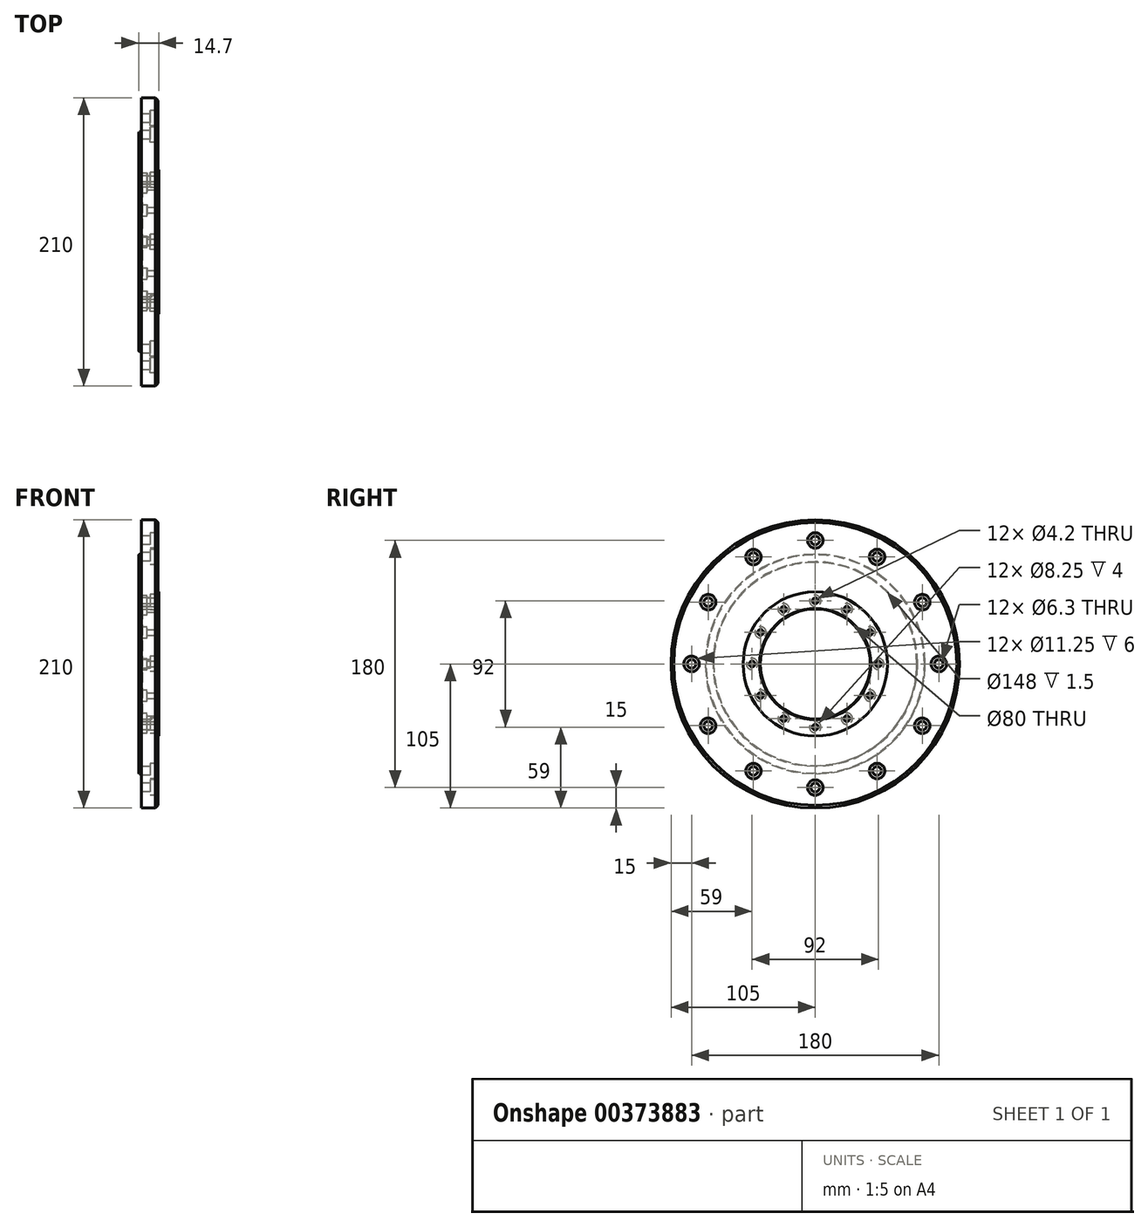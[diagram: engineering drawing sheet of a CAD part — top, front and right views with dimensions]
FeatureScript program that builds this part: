
annotation { "Feature Type Name" : "Feature", "Feature Type Description" : "" }
export const myFeature = defineFeature(function(context is Context, id is Id, definition is map)
    precondition{}
    {
        {
            var Q0;
            Q0=qCreatedBy(makeId("Front.planeOp"),FACE);
            var sketch = newSketch(context, id + "F0", { "sketchPlane" : qUnion([Q0])});
            skLineSegment(sketch, "E0", {"start": v(91.08, 0) * mm, "end": v(-135.26, 0) * mm, "construction": true});
            skLineSegment(sketch, "E1", {"start": v(-4.62, 80) * mm, "end": v(-4.62, 105) * mm});
            skLineSegment(sketch, "E2", {"start": v(-4.62, 105) * mm, "end": v(7.58, 105) * mm});
            skLineSegment(sketch, "E3", {"start": v(7.58, 105) * mm, "end": v(7.58, 52.5) * mm});
            skLineSegment(sketch, "E4", {"start": v(7.58, 52.5) * mm, "end": v(8.08, 52.5) * mm});
            skLineSegment(sketch, "E5", {"start": v(8.08, 52.5) * mm, "end": v(8.08, 40) * mm});
            skLineSegment(sketch, "E6", {"start": v(-4.62, 80) * mm, "end": v(-6.62, 80) * mm});
            skLineSegment(sketch, "E7", {"start": v(8.08, 40) * mm, "end": v(-4.62, 40) * mm});
            skLineSegment(sketch, "E8", {"start": v(-6.62, 80) * mm, "end": v(-6.62, 74) * mm});
            skLineSegment(sketch, "E9", {"start": v(-6.62, 74) * mm, "end": v(-4.62, 74) * mm});
            skLineSegment(sketch, "E10", {"start": v(-4.62, 74) * mm, "end": v(-4.62, 40) * mm});
            skPoint(sketch, "E11.orphan", {"position": v(-6.62, 40) * mm});
            skSolve(sketch);
        }
        {
            var Q0;
            Q0 = qSketchRegion(id + "F0", true);
            var Q1;
            Q1=sQuery(id+"F0.wireOp",EDGE,"E0");
            revolve(context, id + "F1", {"entities" : qUnion([Q0]), "axis" : qUnion([Q1]), "revolveType" : RevolveType.FULL});
        }
        {
            var Q0;
            Q0=makeQuery(id+"F1.opRevolve","SWEPT_FACE",FACE,{"disambiguationData":[OSD([sQuery(id+"F0.wireOp",EDGE,"E1")])]});
            var sketch = newSketch(context, id + "F2", { "sketchPlane" : qUnion([Q0])});
            skPoint(sketch, "E12", {"position": v(0, 0) * mm});
            skPoint(sketch, "E13", {"position": v(0, 46) * mm});
            skPoint(sketch, "E14", {"position": v(23, 39.84) * mm});
            skPoint(sketch, "E15", {"position": v(39.84, 23) * mm});
            skPoint(sketch, "E16", {"position": v(46, 0) * mm});
            skPoint(sketch, "E17", {"position": v(39.84, -23) * mm});
            skPoint(sketch, "E18", {"position": v(23, -39.84) * mm});
            skPoint(sketch, "E19", {"position": v(0, -46) * mm});
            skPoint(sketch, "E20", {"position": v(-23, -39.84) * mm});
            skPoint(sketch, "E21", {"position": v(-39.84, -23) * mm});
            skPoint(sketch, "E22", {"position": v(-46, 0) * mm});
            skPoint(sketch, "E23", {"position": v(-39.84, 23) * mm});
            skPoint(sketch, "E24", {"position": v(-23, 39.84) * mm});
            skSolve(sketch);
        }
        {
            var Q0;
            Q0=makeQuery(id+"F1.opRevolve","SWEPT_FACE",FACE,{"disambiguationData":[OSD([sQuery(id+"F0.wireOp",EDGE,"E3")])]});
            var sketch = newSketch(context, id + "F3", { "sketchPlane" : qUnion([Q0])});
            skPoint(sketch, "E25.center", {"position": v(0, 0) * mm});
            skPoint(sketch, "E26", {"position": v(0, 90) * mm});
            skPoint(sketch, "E27", {"position": v(45, 77.94) * mm});
            skPoint(sketch, "E28", {"position": v(77.94, 45) * mm});
            skPoint(sketch, "E29", {"position": v(90, 0) * mm});
            skPoint(sketch, "E30", {"position": v(77.94, -45) * mm});
            skPoint(sketch, "E31", {"position": v(45, -77.94) * mm});
            skPoint(sketch, "E32", {"position": v(0, -90) * mm});
            skPoint(sketch, "E33", {"position": v(-45, -77.94) * mm});
            skPoint(sketch, "E34", {"position": v(-77.94, -45) * mm});
            skPoint(sketch, "E35", {"position": v(-90, 0) * mm});
            skPoint(sketch, "E36", {"position": v(-77.94, 45) * mm});
            skPoint(sketch, "E37", {"position": v(-45, 77.94) * mm});
            skSolve(sketch);
        }
        {
            var Q0;
            Q0=sQuery(id+"F2.wireOp",VERTEX,"E13");
            var Q1;
            Q1=sQuery(id+"F2.wireOp",VERTEX,"E14");
            var Q2;
            Q2=sQuery(id+"F2.wireOp",VERTEX,"E15");
            var Q3;
            Q3=sQuery(id+"F2.wireOp",VERTEX,"E16");
            var Q4;
            Q4=sQuery(id+"F2.wireOp",VERTEX,"E17");
            var Q5;
            Q5=sQuery(id+"F2.wireOp",VERTEX,"E18");
            var Q6;
            Q6=sQuery(id+"F2.wireOp",VERTEX,"E19");
            var Q7;
            Q7=sQuery(id+"F2.wireOp",VERTEX,"E20");
            var Q8;
            Q8=sQuery(id+"F2.wireOp",VERTEX,"E22");
            var Q9;
            Q9=sQuery(id+"F2.wireOp",VERTEX,"E21");
            var Q10;
            Q10=sQuery(id+"F2.wireOp",VERTEX,"E23");
            var Q11;
            Q11=sQuery(id+"F2.wireOp",VERTEX,"E24");
            var Q12;
            Q12=makeQuery(id+"F1.opRevolve","SWEPT_BODY",BODY,{"disambiguationData":[OSD([sQuery(id+"F0.wireOp",EDGE,"8f36247e-526f-4479-acc4-7eec241f1e58"),sQuery(id+"F0.wireOp",EDGE,"E1"),sQuery(id+"F0.wireOp",EDGE,"E2"),sQuery(id+"F0.wireOp",EDGE,"E3"),sQuery(id+"F0.wireOp",EDGE,"E4"),sQuery(id+"F0.wireOp",EDGE,"E5")])]});
            hole(context, id + "F4", {"style" : HoleStyle.C_BORE, "endStyle" : HoleEndStyle.THROUGH, "standardTappedOrClearance" : lookupTablePath({ "standard" : "ISO", "fit" : "Close", "size" : "M4", "type" : "Clearance" }), "standardBlindInLast" : lookupTablePath({ "fit" : "Close", "standard" : "ISO", "size" : "M4", "type" : "Clearance" }), "holeDiameter" : 4.2 * mm, "cBoreDiameter" : 8.25 * mm, "cBoreDepth" : 4 * mm, "tappedDepth" : 16.82 * mm, "tapClearance" : 3, "locations" : qUnion([Q0, Q1, Q2, Q3, Q4, Q5, Q6, Q7, Q8, Q9, Q10, Q11]), "scope" : qUnion([Q12]), "startStyle" : HoleStartStyle.SKETCH});
        }
        {
            var Q0;
            Q0=sQuery(id+"F3.wireOp",VERTEX,"E26");
            var Q1;
            Q1=sQuery(id+"F3.wireOp",VERTEX,"E27");
            var Q2;
            Q2=sQuery(id+"F3.wireOp",VERTEX,"E28");
            var Q3;
            Q3=sQuery(id+"F3.wireOp",VERTEX,"E29");
            var Q4;
            Q4=sQuery(id+"F3.wireOp",VERTEX,"E30");
            var Q5;
            Q5=sQuery(id+"F3.wireOp",VERTEX,"E31");
            var Q6;
            Q6=sQuery(id+"F3.wireOp",VERTEX,"E32");
            var Q7;
            Q7=sQuery(id+"F3.wireOp",VERTEX,"E33");
            var Q8;
            Q8=sQuery(id+"F3.wireOp",VERTEX,"E34");
            var Q9;
            Q9=sQuery(id+"F3.wireOp",VERTEX,"E35");
            var Q10;
            Q10=sQuery(id+"F3.wireOp",VERTEX,"E36");
            var Q11;
            Q11=sQuery(id+"F3.wireOp",VERTEX,"E37");
            var Q12;
            Q12=makeQuery(id+"F1.opRevolve","SWEPT_BODY",BODY,{"disambiguationData":[OSD([sQuery(id+"F0.wireOp",EDGE,"8f36247e-526f-4479-acc4-7eec241f1e58"),sQuery(id+"F0.wireOp",EDGE,"E1"),sQuery(id+"F0.wireOp",EDGE,"E2"),sQuery(id+"F0.wireOp",EDGE,"E3"),sQuery(id+"F0.wireOp",EDGE,"E4"),sQuery(id+"F0.wireOp",EDGE,"E5")])]});
            hole(context, id + "F5", {"style" : HoleStyle.C_BORE, "endStyle" : HoleEndStyle.THROUGH, "standardTappedOrClearance" : lookupTablePath({ "standard" : "ISO", "fit" : "Close", "size" : "M6", "type" : "Clearance" }), "standardBlindInLast" : lookupTablePath({ "fit" : "Close", "standard" : "ISO", "size" : "M6", "type" : "Clearance" }), "holeDiameter" : 6.3 * mm, "cBoreDiameter" : 11.25 * mm, "cBoreDepth" : 6 * mm, "tappedDepth" : 16.82 * mm, "tapClearance" : 3, "locations" : qUnion([Q0, Q1, Q2, Q3, Q4, Q5, Q6, Q7, Q8, Q9, Q10, Q11]), "scope" : qUnion([Q12]), "startStyle" : HoleStartStyle.SKETCH});
        }
        {
            var Q0;
            Q0=makeQuery(id+"F1.opRevolve","SWEPT_EDGE",EDGE,{"disambiguationData":[OSD([sQuery(id+"F0.wireOp",EDGE,"E2"),sQuery(id+"F0.wireOp",EDGE,"E3")])]});
            chamfer(context, id + "F6", {"entities" : qUnion([Q0]), "width" : 2 * mm, "tangentPropagation" : true});
        }
        {
            var Q0;
            Q0=makeQuery(id+"F1.opRevolve","SWEPT_EDGE",EDGE,{"disambiguationData":[OSD([sQuery(id+"F0.wireOp",EDGE,"E6"),sQuery(id+"F0.wireOp",EDGE,"E8")])]});
            var Q1;
            Q1=makeQuery(id+"F1.opRevolve","SWEPT_EDGE",EDGE,{"disambiguationData":[OSD([sQuery(id+"F0.wireOp",EDGE,"E7"),sQuery(id+"F0.wireOp",EDGE,"E8")])]});
            chamfer(context, id + "F7", {"entities" : qUnion([Q0, Q1]), "width" : .5 * mm, "tangentPropagation" : true});
        }
    });
